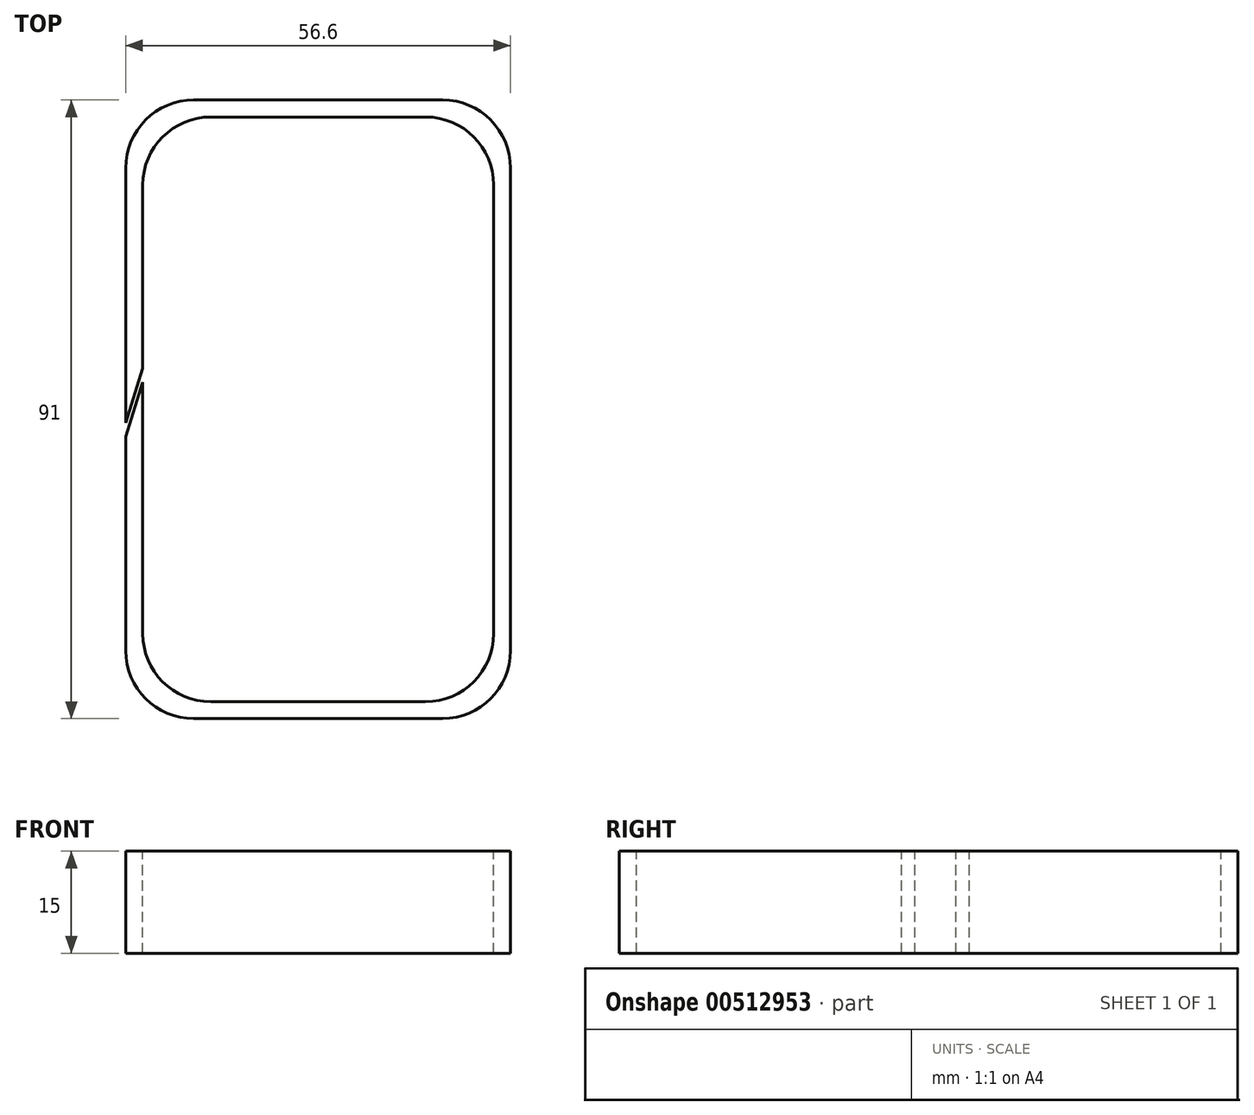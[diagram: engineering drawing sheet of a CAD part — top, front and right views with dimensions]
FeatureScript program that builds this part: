
annotation { "Feature Type Name" : "Feature", "Feature Type Description" : "" }
export const myFeature = defineFeature(function(context is Context, id is Id, definition is map)
    precondition{}
    {
        {
            var Q0;
            Q0=qCreatedBy(makeId("Top.planeOp"),FACE);
            var sketch = newSketch(context, id + "F0", { "sketchPlane" : qUnion([Q0])});
            skLineSegment(sketch, "E0.bottom", {"start": v(28.3, 45.5) * mm, "end": v(-28.3, 45.5) * mm});
            skLineSegment(sketch, "E0.top", {"start": v(28.3, -45.5) * mm, "end": v(-28.3, -45.5) * mm});
            skLineSegment(sketch, "E0.left", {"start": v(28.3, 45.5) * mm, "end": v(28.3, -45.5) * mm});
            skLineSegment(sketch, "E0.right", {"start": v(-28.3, 45.5) * mm, "end": v(-28.3, -45.5) * mm});
            skPoint(sketch, "E0.middle", {"position": v(0, 0) * mm});
            skSolve(sketch);
        }
        {
            var Q0;
            Q0=makeQuery(id+"F0.imprint","IMPRINT",FACE,{"disambiguationData":[TD([[makeQuery(id+"F0.imprint","IMPRINT",EDGE,{"derivedFrom":sQuery(id+"F0.wireOp",EDGE,"E0.bottom")}),1.0]])]});
            extrude(context, id + "F1", {"entities" : qUnion([Q0]), "depth" : 15 * mm});
        }
        {
            var Q0;
            Q0=makeQuery(id+"F1.opExtrude","CAP_FACE",FACE,{"disambiguationData":[OSD([sQuery(id+"F0.wireOp",EDGE,"E0.bottom"),sQuery(id+"F0.wireOp",EDGE,"E0.top"),sQuery(id+"F0.wireOp",EDGE,"E0.left"),sQuery(id+"F0.wireOp",EDGE,"E0.right")])],"isStart":false});
            var sketch = newSketch(context, id + "F2", { "sketchPlane" : qUnion([Q0])});
            skLineSegment(sketch, "E1.bottom", {"start": v(25.8, -43) * mm, "end": v(-25.8, -43) * mm});
            skLineSegment(sketch, "E1.top", {"start": v(25.8, 43) * mm, "end": v(-25.8, 43) * mm});
            skLineSegment(sketch, "E1.left", {"start": v(25.8, -43) * mm, "end": v(25.8, 43) * mm});
            skLineSegment(sketch, "E1.right", {"start": v(-25.8, -43) * mm, "end": v(-25.8, 43) * mm});
            skPoint(sketch, "E1.middle", {"position": v(0, 0) * mm});
            skSolve(sketch);
        }
        {
            var Q0;
            Q0=makeQuery(id+"F2.imprint","IMPRINT",FACE,{"disambiguationData":[TD([[makeQuery(id+"F2.imprint","IMPRINT",EDGE,{"derivedFrom":sQuery(id+"F2.wireOp",EDGE,"E1.bottom")}),-1.0]])]});
            extrude(context, id + "F3", {"entities" : qUnion([Q0]), "operationType" : NewBodyOperationType.REMOVE, "oppositeDirection" : true, "depth" : 25 * mm});
        }
        {
            var Q0;
            Q0=makeQuery(id+"F1.opExtrude","SWEPT_EDGE",EDGE,{"disambiguationData":[OSD([sQuery(id+"F0.wireOp",EDGE,"E0.top"),sQuery(id+"F0.wireOp",EDGE,"E0.left")])]});
            var Q1;
            Q1=makeQuery(id+"F1.opExtrude","SWEPT_EDGE",EDGE,{"disambiguationData":[OSD([sQuery(id+"F0.wireOp",EDGE,"E0.bottom"),sQuery(id+"F0.wireOp",EDGE,"E0.left")])]});
            var Q2;
            Q2=makeQuery(id+"F1.opExtrude","SWEPT_EDGE",EDGE,{"disambiguationData":[OSD([sQuery(id+"F0.wireOp",EDGE,"E0.top"),sQuery(id+"F0.wireOp",EDGE,"E0.right")])]});
            var Q3;
            Q3=makeQuery(id+"F1.opExtrude","SWEPT_EDGE",EDGE,{"disambiguationData":[OSD([sQuery(id+"F0.wireOp",EDGE,"E0.bottom"),sQuery(id+"F0.wireOp",EDGE,"E0.right")])]});
            var Q4;
            Q4=makeQuery(id+"F3.boolean.opBoolean","COPY",EDGE,{"derivedFrom":makeQuery(id+"F3.opExtrude","SWEPT_EDGE",EDGE,{"disambiguationData":[OSD([sQuery(id+"F2.wireOp",EDGE,"E1.top"),sQuery(id+"F2.wireOp",EDGE,"E1.left")])]})});
            var Q5;
            Q5=makeQuery(id+"F3.boolean.opBoolean","COPY",EDGE,{"derivedFrom":makeQuery(id+"F3.opExtrude","SWEPT_EDGE",EDGE,{"disambiguationData":[OSD([sQuery(id+"F2.wireOp",EDGE,"E1.top"),sQuery(id+"F2.wireOp",EDGE,"E1.right")])]})});
            var Q6;
            Q6=makeQuery(id+"F3.boolean.opBoolean","COPY",EDGE,{"derivedFrom":makeQuery(id+"F3.opExtrude","SWEPT_EDGE",EDGE,{"disambiguationData":[OSD([sQuery(id+"F2.wireOp",EDGE,"E1.bottom"),sQuery(id+"F2.wireOp",EDGE,"E1.right")])]})});
            var Q7;
            Q7=makeQuery(id+"F3.boolean.opBoolean","COPY",EDGE,{"derivedFrom":makeQuery(id+"F3.opExtrude","SWEPT_EDGE",EDGE,{"disambiguationData":[OSD([sQuery(id+"F2.wireOp",EDGE,"E1.bottom"),sQuery(id+"F2.wireOp",EDGE,"E1.left")])]})});
            fillet(context, id + "F4", {"entities" : qUnion([Q0, Q1, Q2, Q3, Q4, Q5, Q6, Q7]), "radius" : 10 * mm, "tangentPropagation" : true, "allowEdgeOverflow" : false});
        }
        {
            var Q0;
            Q0=makeQuery(id+"F1.opExtrude","CAP_FACE",FACE,{"disambiguationData":[OSD([sQuery(id+"F0.wireOp",EDGE,"E0.bottom"),sQuery(id+"F0.wireOp",EDGE,"E0.top"),sQuery(id+"F0.wireOp",EDGE,"E0.left"),sQuery(id+"F0.wireOp",EDGE,"E0.right")])],"isStart":false});
            var sketch = newSketch(context, id + "F5", { "sketchPlane" : qUnion([Q0])});
            skLineSegment(sketch, "E2", {"start": v(-28.3, -4) * mm, "end": v(-25.8, 4) * mm});
            skLineSegment(sketch, "E3", {"start": v(-28.3, -2) * mm, "end": v(-25.8, 6) * mm});
            skSolve(sketch);
        }
        {
            var Q0;
            {var subQ0=sQuery(id+"F5.wireOp",EDGE,"E2");Q0=makeQuery(id+"F5.imprint","IMPRINT",FACE,{"disambiguationData":[TD([[makeQuery(id+"F5.imprint","IMPRINT",EDGE,{"derivedFrom":subQ0}),1.0]])]});}
            extrude(context, id + "F6", {"entities" : qUnion([Q0]), "operationType" : NewBodyOperationType.REMOVE, "oppositeDirection" : true, "depth" : 25 * mm});
        }
    });
